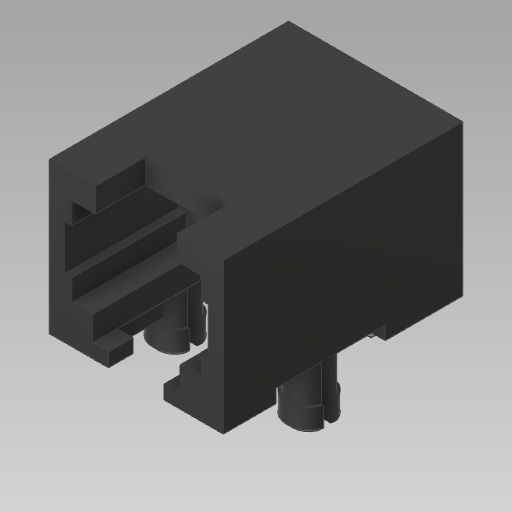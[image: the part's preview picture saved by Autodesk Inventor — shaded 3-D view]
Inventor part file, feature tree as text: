
AUTODESK INVENTOR PART (.ipt)
format: ipt  version: 2020 (Build 240168000, 168)  size: 302,592 bytes
history: native  units: in
note: dims shown in document units (in); Inventor stores cm internally (conversion verified against a paired STEP export)
features: sketch x9, extrude x7, plane x2, revolve x2, chamfer x1
ambient origin geometry x8: Origin, YZ Plane, XZ Plane, XY Plane, X Axis, Y Axis, Z Axis, Center Point
bodies: Solid1 (feature_tree)
feature tree (21):
  extrude  "Extrusion1"  Depth=0.45in
  extrude  "Extrusion2"  Depth=0.0725in
  extrude  "Extrusion3"  Depth=0.215in
  extrude  "Extrusion4"  Depth=0.073in
  extrude  "Extrusion5"  Depth=0.137in
  plane  "Work Plane1"
  plane  "Work Plane2"
  revolve  "Revolution1"  [1 undecoded]
  revolve  "Revolution2"  [1 undecoded]
  extrude  "Extrusion6"  Depth=0.0735in
  extrude  "Extrusion7"  Depth=0.357in
  chamfer  "Chamfer1"  Distance=0.259in
  sketch  "Sketch1"  dims[d0=0.52in d1=0.45in]
  sketch  "Sketch2"  dims[d2=0.715in d3=0.0in d17=0.0725in]
  sketch  "Sketch3"  dims[d18=0.1925in d19=0.215in]
  sketch  "Sketch4"  dims[d20=0.041in d21=0.073in]
  sketch  "Sketch5"  dims[d22=0.177in d23=0.137in]
  sketch  "Sketch6"  dims[d24=0.1305in d25=0.341in d26=0.0in]
  sketch  "Sketch7"  dims[d27=0.245in d28=0.15in]
  sketch  "Sketch8"  dims[d29=0.341in d30=0.0in d31=0.0735in]
  sketch  "Sketch9"  dims[d32=0.166in d33=0.357in d34=0.259in d35=0.341in d36=0.0in d38=0.22in d39=0.044in d41=0.326in d42=0.045in d43=0.177in d44=0.045in d45=0.054in d46=0.415in d47=0.04in d48=0.0in d49=0.2in d50=-0.2in d51=0.06in d53=0.066in d54=45.0deg d55=0.05in d58=0.1875in d59=0.058in d60=0.256in d61=90.0deg d62=0.06in d63=0.066in d64=45.0deg d65=0.05in d66=0.1875in d67=0.058in d68=0.256in d69=90.0deg d70=0.039in d71=0.04in d72=0.0in d73=0.13in d74=0.1in d75=0.05in d76=0.144in d77=0.025in d78=1.1811in d80=0.1in d81=0.3937in d83=1.0in d85=0.1in d86=0.05in d87=0.0in d88=0.0in d89=0.01in d90=0.125in d91=45.0deg]
note: 2 required parameter values undecoded (feature->parameter linkage not recoverable at this tier; creation-order binding heuristic only, values carry confidence <= 0.55)
